# Revit family: MechanicalEquipment_HotWater_Rheem_TankpakSeries2_TPE09-B
name_source: partatom
category: Mechanical Equipment
units: mm (PartAtom-declared; Revit-internal decimal feet)

## family parameters
Always vertical = Yes
Cut with Voids When Loaded = No
Part Type = Normal
Room Calculation Point = No
Round Connector Dimension = Use Diameter
Shared = No
Work Plane-Based = No

## types (2) — shared parameters
ApparentLoad_ANZRS = 2736 VA
Assembly Code = D3020100
BaseToController = 1000 mm  [stored 3.28084 ft]
BaseToGPO = 850 mm  [stored 2.78871 ft]
ClearanceZoneWidth = 800 mm  [stored 2.62467 ft]
ColdPipeDescription = Cold Water In
ColdPipeRadius = 25 mm  [stored 0.082021 ft]
ColdPipeSize = 50 mm  [stored 0.164042 ft]
ControllerConnectorDescription = Electrical Connector
ControllerHeight = 300 mm
ControllerMaterial = Controller Material
ControllerTextMaterial = Controller Text Material
Description = Tankpak Series 2 external 09 Back to Back
ElectricalConnectionInformation = Each water heater is supplied with a 1.8 metre lead and plug and requires a 240 V 50 Hz switched general purpose outlet (GPO) to be located within 1.2 metres of the installation. The GPO must be clear of the flue exhaust, draining water, gas supply pipe and water connections. The GPO must be suitable for outdoor installation if installed outdoors.
ElectricalConnectionType = Hard Wired Conduit Connection
ElectricalPowerConsumption = 80 Watts - 872/862 series - Burner on. anti-frost device inactive;175 Watts - 872627 (outdoor) - Burner on. anti-frost device active;187 Watts - 862627 (indoor) - Burner on. anti-frost device active.
FirstHourCapacity = 8220 l
FlueSize = 250 mm  [stored 0.82021 ft]
FlueTankMaterial = Flue Tank Material
FrameMaterial = Frame Material
FrameThickness = 160 mm  [stored 0.524934 ft]
Frequency_ANZRS = 50 Hz
GasPipeSize = 65 mm  [stored 0.213255 ft]
GasXReference = 439 mm
GasYReference = 269 mm
GpoHeight = 300 mm
GpoMaterial = Gpo Material
Height = 1741 mm  [stored 5.71194 ft]
HotPipeDescription = Hot Water Out
HotPipeSize = 50 mm  [stored 0.164042 ft]
HotXReference = 399 mm
HotYReference = 392 mm  [stored 1.28609 ft]
Manufacturer = Rheem
Model = TPE09
ModifiedIssue_ANZRS = 20141010.54 $
PowerFactor_ANZRS = 1
PumpLength = 300 mm
PumpMaterial = Pump Material
PumpRadius = 85 mm  [stored 0.278871 ft]
PumpXReference = 571 mm  [stored 1.87336 ft]
PumpYReference = 160 mm  [stored 0.524934 ft]
RecommendedStorage = 2 x 610430@410L
RowLength = 1120 mm
StandThickness = 90 mm
TankCentreXReference = 380 mm
TankDistance = 596 mm
TankHeight = 500 mm  [stored 1.64042 ft]
TankThickness = 218 mm
TankWidth = 350 mm
ThermalInput_PerHour = 1845000000 J
TopOfFrame = 1626 mm  [stored 5.33465 ft]
Type Comments = 7405L/hr Recovery @ 50˚C rise
URL = http://www.rheem.com.au
UnitType = Outdoor
Voltage = 240 V
Weight(kg) = 429
Width = 2239 mm

## per-type parameters (varying)
| type | GasPipeDescription |
| TPE09PBD | Propane gas |
| TPE09NBD | Natural gas |

note: [stored X ft] marks values corroborated as IEEE doubles in the binary element streams (Revit-internal decimal feet)

## geometry (parser evidence)
native form markers: Sweep x7
no freeform markers — native parametric forms only
